# Revit family: Pump_Commercial-Effluent-Zoeller-6260_Series
name_source: partatom
category: Mechanical Equipment
revit_build: Autodesk Revit 2018 (Build: 20170223_1515(x64)
units: mm (PartAtom-declared; Revit-internal decimal feet)

## family parameters
Always vertical = No
Cut with Voids When Loaded = No
OmniClass Number = 23.60.30.21
OmniClass Title = Pumps
Part Type = Normal
Room Calculation Point = No
Round Connector Dimension = Use Radius
Shared = Yes
Work Plane-Based = Yes

## types (6) — shared parameters
Assembly Code = D2010900
Default Elevation = 0"
Description = Commercial Duty Pump 6260 Series
Discharge Diameter = VERTICAL 2-inch NPT  THREAD
Discharge Height = 6 7/16"
Discharge Radius = 1"
Height = 14 1/4"
Hertz = 60
Installation Type = Floor Mounted
Insulation = Class A or B
Length = 13 1/8"
Manufacturer = Zoeller
Masterformat Number = 33 36 16
Masterformat Title = Utility Septic Tank Effluent Pumps
Material = Cast Iron-Zoeller-Powder Coated Epoxy
Max. Flow at Min. Head = 115 GPM @ 5'
Max. Water Temp. = 130 °F
Maximum Head = 246"
Minimum Head = 60"
Model = 6267
Motor = 1/2 HP
Motor Thermal Shutoff = Thermal Overload Sensors With Automatic Reset.
Motor Type = Submersible
O-Rings and Cover Gasket = Viton
Omniclass Table 23 Code = 23.60.30.21
Omniclass Table 23 Title = Pumps
Operation = Non-Automatic
Price = Prices may vary. Please consult Manufacturer Representative for most up-to-date price list.
Product Page URL = https://www.zoellerengineered.com
RPM = 1750
Shaft Seal = Silicon Crbide (Rotary)/Carbon (Stationary)
Solid Size = 2"
Type SOW Power Cord Length = 180"
URL = http://www.zoellerpumps.com
Warranty Information = 36 Months (Limited)
Waste Connection = Yes
Width = 11 7/32"

## per-type parameters (varying)
| type | Amps | Impeller Type | Phase | Type | Voltage |
| 6267 - 115V 1Ph | 10.4 | Plastic Vortex | 1 | Split Capacitor | 115 V |
| 6267 - 230V 1Ph | 4.7 | Plastic Vortex | 1 | Split Capacitor | 230 V |
| 6267 - 200V 1Ph | 6.2 | Plastic Vortex | 1 | Split Capacitor | 200 V |
| 6267 - 200V 3Ph | 3.3 | Cast Iron Vortex | 3 | 3 Phase | 200 V |
| 6267 - 230V 3Ph | 3.0 | Cast Iron Vortex | 3 | 3 Phase | 230 V |
| 6267 - 460V 3Ph | 1.5 | Cast Iron Vortex | 3 | 3 Phase | 460 V |

## geometry (parser evidence)
native form markers: Sweep x3
no freeform markers — native parametric forms only
